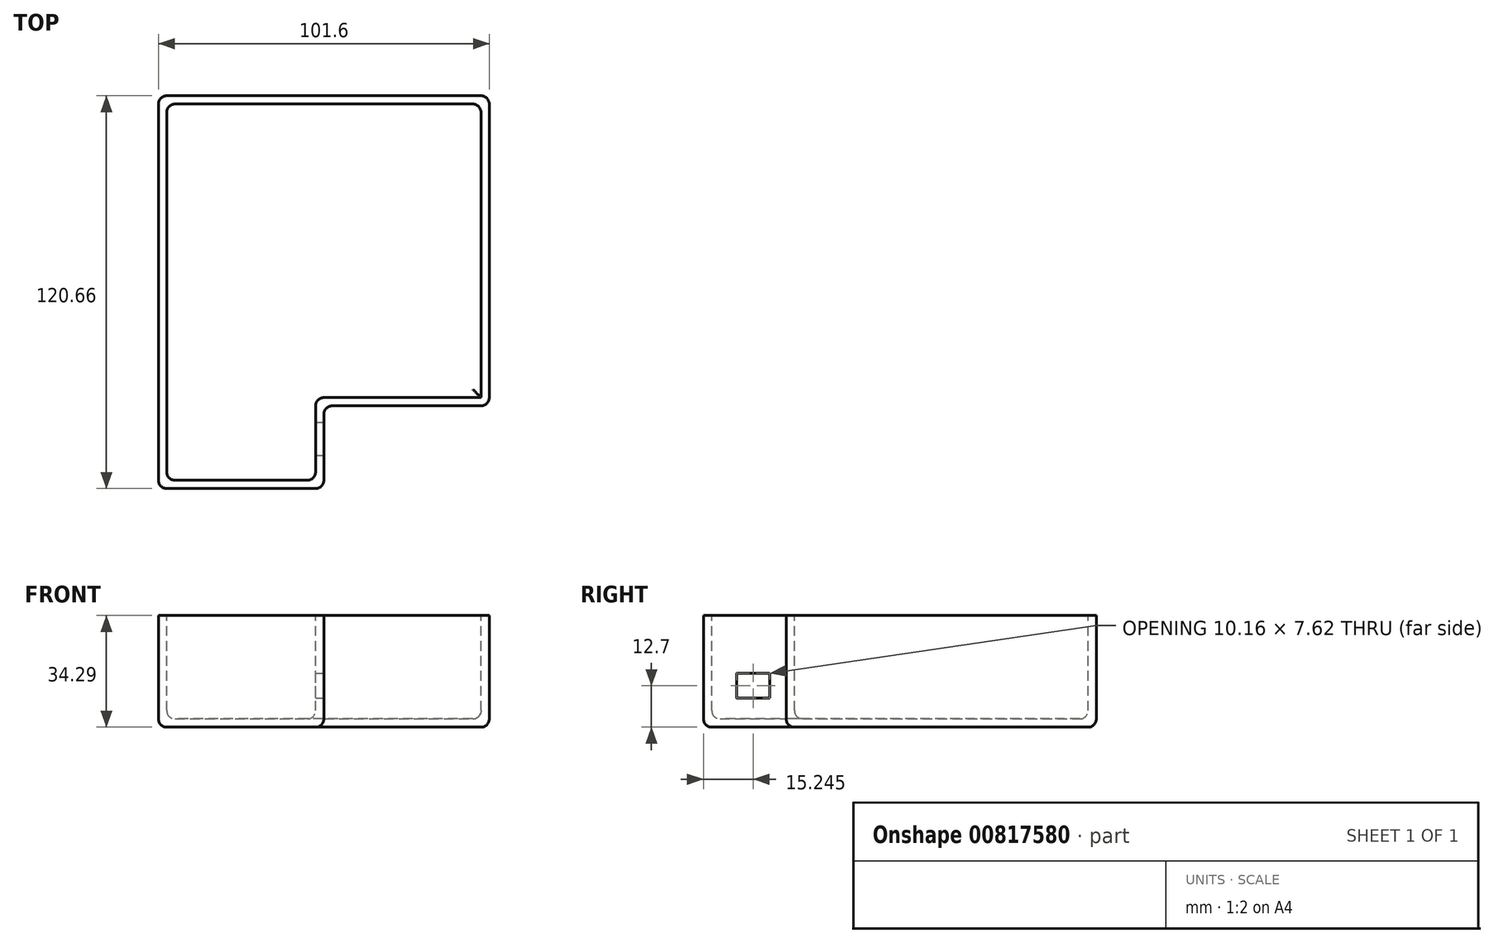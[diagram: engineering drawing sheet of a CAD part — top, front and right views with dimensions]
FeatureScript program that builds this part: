
annotation { "Feature Type Name" : "Feature", "Feature Type Description" : "" }
export const myFeature = defineFeature(function(context is Context, id is Id, definition is map)
    precondition{}
    {
        {
            var Q0;
            Q0=qCreatedBy(makeId("Top.planeOp"),FACE);
            var sketch = newSketch(context, id + "F0", { "sketchPlane" : qUnion([Q0])});
            skLineSegment(sketch, "E0.bottom", {"start": v(-50.8, 60.33) * mm, "end": v(50.8, 60.33) * mm});
            skLineSegment(sketch, "E0.top", {"start": v(-50.8, -60.33) * mm, "end": v(0, -60.33) * mm});
            skLineSegment(sketch, "E0.left", {"start": v(-50.8, 60.33) * mm, "end": v(-50.8, -60.33) * mm});
            skLineSegment(sketch, "E0.right", {"start": v(50.8, 60.33) * mm, "end": v(50.8, -34.92) * mm});
            skPoint(sketch, "E0.middle", {"position": v(0, 0) * mm});
            skLineSegment(sketch, "E1.bottom", {"start": v(50.8, -34.93) * mm, "end": v(0, -34.93) * mm});
            skLineSegment(sketch, "E1.right", {"start": v(0, -34.93) * mm, "end": v(0, -60.33) * mm});
            skPoint(sketch, "E2.orphan", {"position": v(50.8, -60.33) * mm});
            skSolve(sketch);
        }
        {
            var Q0;
            Q0 = qSketchRegion(id + "F0", true);
            extrude(context, id + "F1", {"entities" : qUnion([Q0]), "depth" : 34.3 * mm, "offsetDistance" : 25.4 * mm});
        }
        {
            var Q0;
            Q0=makeQuery(id+"F1.opExtrude","CAP_FACE",FACE,{"disambiguationData":[OSD([sQuery(id+"F0.wireOp",EDGE,"E0.bottom"),sQuery(id+"F0.wireOp",EDGE,"E0.top"),sQuery(id+"F0.wireOp",EDGE,"E0.left"),sQuery(id+"F0.wireOp",EDGE,"E0.right")])],"isStart":false});
            var sketch = newSketch(context, id + "F2", { "sketchPlane" : qUnion([Q0])});
            skLineSegment(sketch, "E3.0", {"start": v(48.26, 57.79) * mm, "end": v(-48.26, 57.79) * mm});
            skLineSegment(sketch, "E3.1", {"start": v(-48.26, -57.79) * mm, "end": v(-2.54, -57.79) * mm});
            skLineSegment(sketch, "E3.2", {"start": v(-2.54, -57.79) * mm, "end": v(-2.54, -32.39) * mm});
            skLineSegment(sketch, "E3.3", {"start": v(-48.26, 57.79) * mm, "end": v(-48.26, -57.79) * mm});
            skLineSegment(sketch, "E3.4", {"start": v(-2.54, -32.39) * mm, "end": v(48.26, -32.39) * mm});
            skLineSegment(sketch, "E3.5", {"start": v(48.26, -32.39) * mm, "end": v(48.26, 57.79) * mm});
            skSolve(sketch);
        }
        {
            var Q0;
            Q0 = qSketchRegion(id + "F2", true);
            extrude(context, id + "F3", {"entities" : qUnion([Q0]), "operationType" : NewBodyOperationType.REMOVE, "oppositeDirection" : true, "depth" : 31.75 * mm, "offsetDistance" : 25.4 * mm});
        }
        {
            var Q0;
            Q0=makeQuery(id+"F1.opExtrude","SWEPT_FACE",FACE,{"disambiguationData":[OSD([sQuery(id+"F0.wireOp",EDGE,"E1.right")])]});
            var sketch = newSketch(context, id + "F4", { "sketchPlane" : qUnion([Q0])});
            skLineSegment(sketch, "E4.bottom", {"start": v(-50.16, 16.51) * mm, "end": v(-40, 16.51) * mm});
            skLineSegment(sketch, "E4.top", {"start": v(-50.16, 8.9) * mm, "end": v(-40, 8.9) * mm});
            skLineSegment(sketch, "E4.left", {"start": v(-50.16, 16.51) * mm, "end": v(-50.16, 8.9) * mm});
            skLineSegment(sketch, "E4.right", {"start": v(-40, 16.51) * mm, "end": v(-40, 8.9) * mm});
            skPoint(sketch, "E4.middle", {"position": v(-45.09, 12.7) * mm});
            skSolve(sketch);
        }
        {
            var Q0;
            Q0 = qSketchRegion(id + "F4", true);
            extrude(context, id + "F5", {"entities" : qUnion([Q0]), "operationType" : NewBodyOperationType.REMOVE, "endBound" : BoundingType.UP_TO_NEXT, "oppositeDirection" : true, "depth" : 25.4 * mm, "offsetDistance" : 25.4 * mm});
        }
        {
            var Q0;
            Q0=makeQuery(id+"F5.boolean.opBoolean","COPY",EDGE,{"derivedFrom":makeQuery(id+"F5.opExtrude","SWEPT_EDGE",EDGE,{"disambiguationData":[OSD([sQuery(id+"F4.wireOp",EDGE,"E4.bottom"),sQuery(id+"F4.wireOp",EDGE,"E4.left")])]})});
            var Q1;
            Q1=makeQuery(id+"F5.boolean.opBoolean","COPY",EDGE,{"derivedFrom":makeQuery(id+"F5.opExtrude","SWEPT_EDGE",EDGE,{"disambiguationData":[OSD([sQuery(id+"F4.wireOp",EDGE,"E4.bottom"),sQuery(id+"F4.wireOp",EDGE,"E4.right")])]})});
            var Q2;
            Q2=makeQuery(id+"F5.boolean.opBoolean","COPY",EDGE,{"derivedFrom":makeQuery(id+"F5.opExtrude","SWEPT_EDGE",EDGE,{"disambiguationData":[OSD([sQuery(id+"F4.wireOp",EDGE,"E4.top"),sQuery(id+"F4.wireOp",EDGE,"E4.right")])]})});
            var Q3;
            Q3=makeQuery(id+"F5.boolean.opBoolean","COPY",EDGE,{"derivedFrom":makeQuery(id+"F5.opExtrude","SWEPT_EDGE",EDGE,{"disambiguationData":[OSD([sQuery(id+"F4.wireOp",EDGE,"E4.top"),sQuery(id+"F4.wireOp",EDGE,"E4.left")])]})});
            fillet(context, id + "F6", {"entities" : qUnion([Q0, Q1, Q2, Q3]), "radius" : 0.13 * mm, "tangentPropagation" : true, "allowEdgeOverflow" : false});
        }
        {
            var Q0;
            Q0=makeQuery(id+"F1.opExtrude","SWEPT_EDGE",EDGE,{"disambiguationData":[OSD([sQuery(id+"F0.wireOp",EDGE,"E0.right"),sQuery(id+"F0.wireOp",EDGE,"E1.bottom")])]});
            var Q1;
            Q1=makeQuery(id+"F1.opExtrude","SWEPT_EDGE",EDGE,{"disambiguationData":[OSD([sQuery(id+"F0.wireOp",EDGE,"E1.bottom"),sQuery(id+"F0.wireOp",EDGE,"E1.right")])]});
            var Q2;
            Q2=makeQuery(id+"F1.opExtrude","SWEPT_EDGE",EDGE,{"disambiguationData":[OSD([sQuery(id+"F0.wireOp",EDGE,"E0.top"),sQuery(id+"F0.wireOp",EDGE,"E1.right")])]});
            var Q3;
            Q3=makeQuery(id+"F3.boolean.opBoolean","COPY",EDGE,{"derivedFrom":makeQuery(id+"F3.opExtrude","SWEPT_EDGE",EDGE,{"disambiguationData":[OSD([sQuery(id+"F2.wireOp",EDGE,"E3.2"),sQuery(id+"F2.wireOp",EDGE,"E3.4")])]})});
            var Q4;
            Q4=makeQuery(id+"F1.opExtrude","SWEPT_EDGE",EDGE,{"disambiguationData":[OSD([sQuery(id+"F0.wireOp",EDGE,"E0.top"),sQuery(id+"F0.wireOp",EDGE,"E0.left")])]});
            var Q5;
            Q5=makeQuery(id+"F3.boolean.opBoolean","COPY",EDGE,{"derivedFrom":makeQuery(id+"F3.opExtrude","SWEPT_EDGE",EDGE,{"disambiguationData":[OSD([sQuery(id+"F2.wireOp",EDGE,"E3.1"),sQuery(id+"F2.wireOp",EDGE,"E3.2")])]})});
            var Q6;
            Q6=makeQuery(id+"F3.boolean.opBoolean","COPY",EDGE,{"derivedFrom":makeQuery(id+"F3.opExtrude","SWEPT_EDGE",EDGE,{"disambiguationData":[OSD([sQuery(id+"F2.wireOp",EDGE,"E3.1"),sQuery(id+"F2.wireOp",EDGE,"E3.3")])]})});
            var Q7;
            Q7=makeQuery(id+"F1.opExtrude","SWEPT_EDGE",EDGE,{"disambiguationData":[OSD([sQuery(id+"F0.wireOp",EDGE,"E0.bottom"),sQuery(id+"F0.wireOp",EDGE,"E0.right")])]});
            var Q8;
            Q8=makeQuery(id+"F3.boolean.opBoolean","COPY",EDGE,{"derivedFrom":makeQuery(id+"F3.opExtrude","SWEPT_EDGE",EDGE,{"disambiguationData":[OSD([sQuery(id+"F2.wireOp",EDGE,"E3.0"),sQuery(id+"F2.wireOp",EDGE,"E3.5")])]})});
            var Q9;
            Q9=makeQuery(id+"F3.boolean.opBoolean","COPY",EDGE,{"derivedFrom":makeQuery(id+"F3.opExtrude","SWEPT_EDGE",EDGE,{"disambiguationData":[OSD([sQuery(id+"F2.wireOp",EDGE,"E3.0"),sQuery(id+"F2.wireOp",EDGE,"E3.3")])]})});
            var Q10;
            Q10=makeQuery(id+"F1.opExtrude","SWEPT_EDGE",EDGE,{"disambiguationData":[OSD([sQuery(id+"F0.wireOp",EDGE,"E0.bottom"),sQuery(id+"F0.wireOp",EDGE,"E0.left")])]});
            var Q11;
            Q11=makeQuery(id+"F1.opExtrude","CAP_FACE",FACE,{"disambiguationData":[OSD([sQuery(id+"F0.wireOp",EDGE,"E0.bottom"),sQuery(id+"F0.wireOp",EDGE,"E0.top"),sQuery(id+"F0.wireOp",EDGE,"E0.left"),sQuery(id+"F0.wireOp",EDGE,"E0.right"),sQuery(id+"F0.wireOp",EDGE,"E1.bottom"),sQuery(id+"F0.wireOp",EDGE,"E1.right")])],"isStart":true});
            var Q12;
            Q12=makeQuery(id+"F3.boolean.opBoolean","COPY",FACE,{"derivedFrom":makeQuery(id+"F3.opExtrude","CAP_FACE",FACE,{"disambiguationData":[OSD([sQuery(id+"F2.wireOp",EDGE,"E3.0"),sQuery(id+"F2.wireOp",EDGE,"E3.1"),sQuery(id+"F2.wireOp",EDGE,"E3.2"),sQuery(id+"F2.wireOp",EDGE,"E3.3"),sQuery(id+"F2.wireOp",EDGE,"E3.4"),sQuery(id+"F2.wireOp",EDGE,"E3.5")])],"isStart":false})});
            fillet(context, id + "F7", {"entities" : qUnion([Q0, Q1, Q2, Q3, Q4, Q5, Q6, Q7, Q8, Q9, Q10, Q11, Q12]), "radius" : 2.54 * mm, "tangentPropagation" : true, "allowEdgeOverflow" : false});
        }
    });
